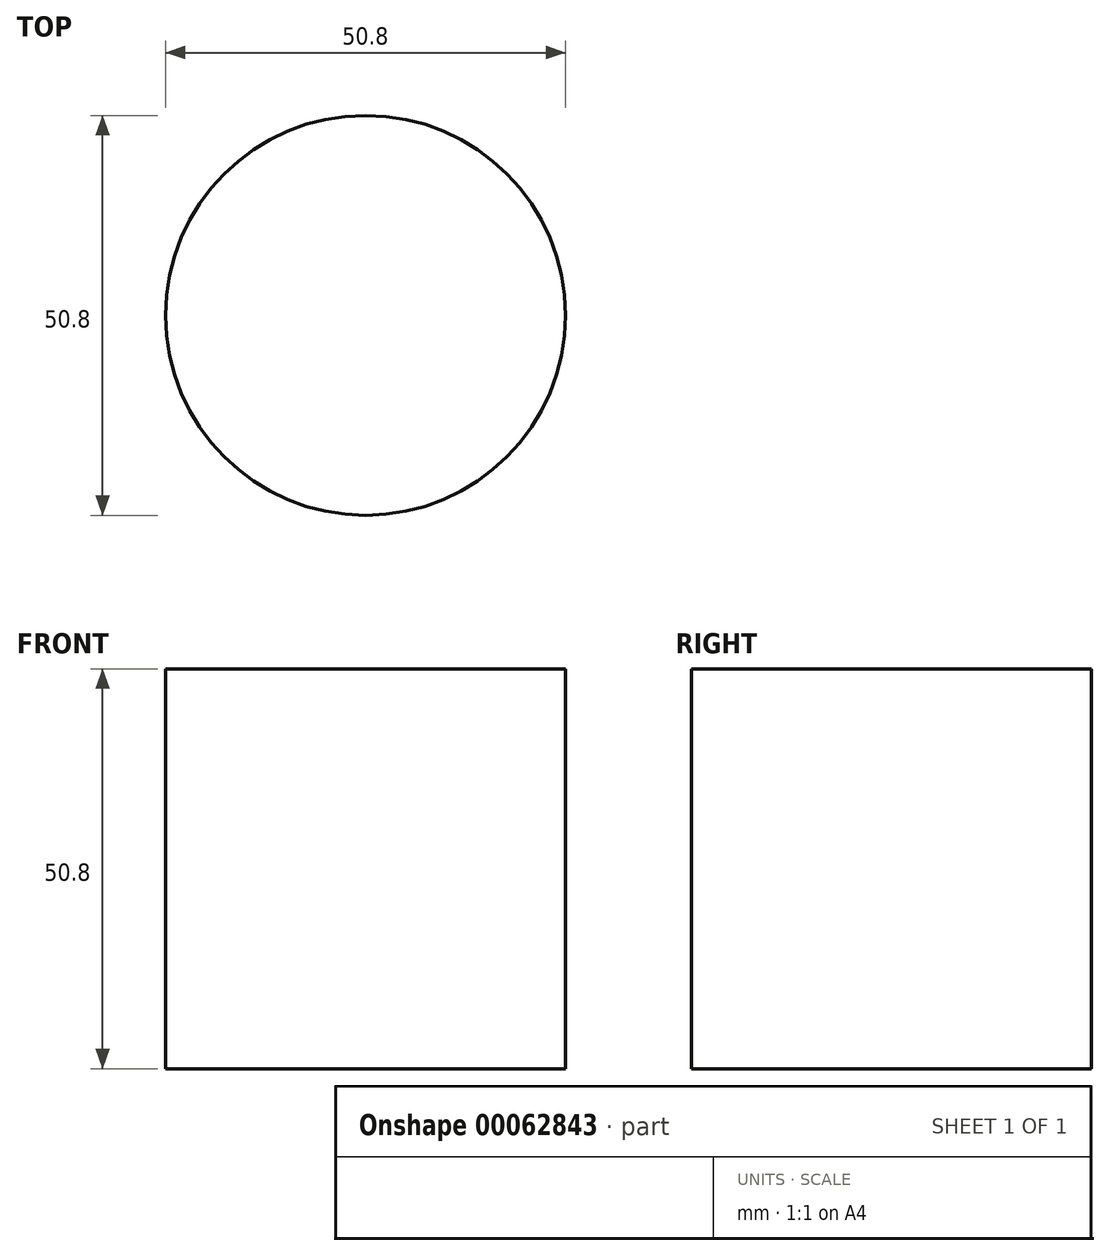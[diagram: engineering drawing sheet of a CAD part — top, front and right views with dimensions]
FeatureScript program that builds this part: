
annotation { "Feature Type Name" : "Feature", "Feature Type Description" : "" }
export const myFeature = defineFeature(function(context is Context, id is Id, definition is map)
    precondition{}
    {
        {
            var Q0;
            Q0=qCreatedBy(makeId("Top.planeOp"),FACE);
            var sketch = newSketch(context, id + "F0", { "sketchPlane" : qUnion([Q0])});
            skCircle(sketch, "E0", {"center": v(0, 0) * mm, "radius": 25.4 * mm});
            skPoint(sketch, "E1", {"position": v(0, 25.4) * mm});
            skSolve(sketch);
        }
        {
            var Q0;
            Q0=makeQuery(id+"F0.imprint","IMPRINT",FACE,{"disambiguationData":[TD([[makeQuery(id+"F0.imprint","IMPRINT",EDGE,{"derivedFrom":sQuery(id+"F0.wireOp",EDGE,"E0")}),1.0]])]});
            extrude(context, id + "F1", {"entities" : qUnion([Q0]), "endBound" : BoundingType.SYMMETRIC, "depth" : 50.8 * mm});
        }
    });
